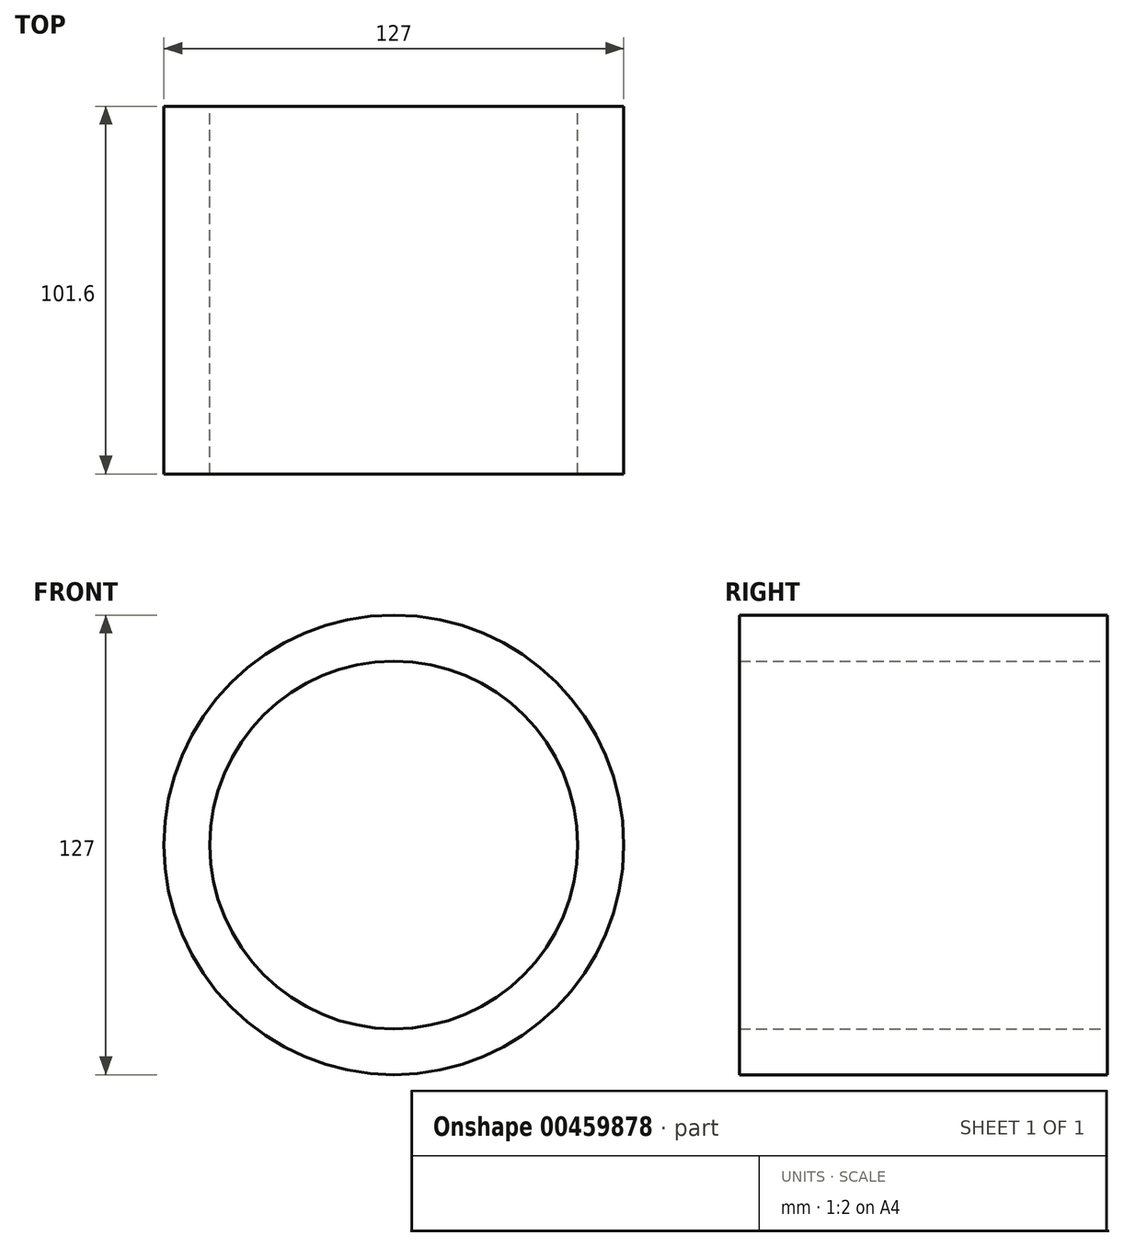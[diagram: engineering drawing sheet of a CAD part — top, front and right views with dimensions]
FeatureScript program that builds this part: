
annotation { "Feature Type Name" : "Feature", "Feature Type Description" : "" }
export const myFeature = defineFeature(function(context is Context, id is Id, definition is map)
    precondition{}
    {
        {
            var Q0;
            Q0=qCreatedBy(makeId("Front.planeOp"),FACE);
            var sketch = newSketch(context, id + "F0", { "sketchPlane" : qUnion([Q0])});
            skCircle(sketch, "E0", {"center": v(0, 0) * mm, "radius": 38.1 * mm});
            skCircle(sketch, "E1", {"center": v(0, 0) * mm, "radius": 50.8 * mm});
            skCircle(sketch, "E2", {"center": v(0, 0) * mm, "radius": 63.5 * mm});
            skSolve(sketch);
        }
        {
            var Q0;
            Q0=makeQuery(id+"F0.imprint","IMPRINT",FACE,{"disambiguationData":[TD([[makeQuery(id+"F0.imprint","IMPRINT",EDGE,{"derivedFrom":sQuery(id+"F0.wireOp",EDGE,"E1")}),-1.0]])]});
            extrude(context, id + "F1", {"entities" : qUnion([Q0]), "endBound" : BoundingType.SYMMETRIC, "depth" : 101.6 * mm});
        }
    });
